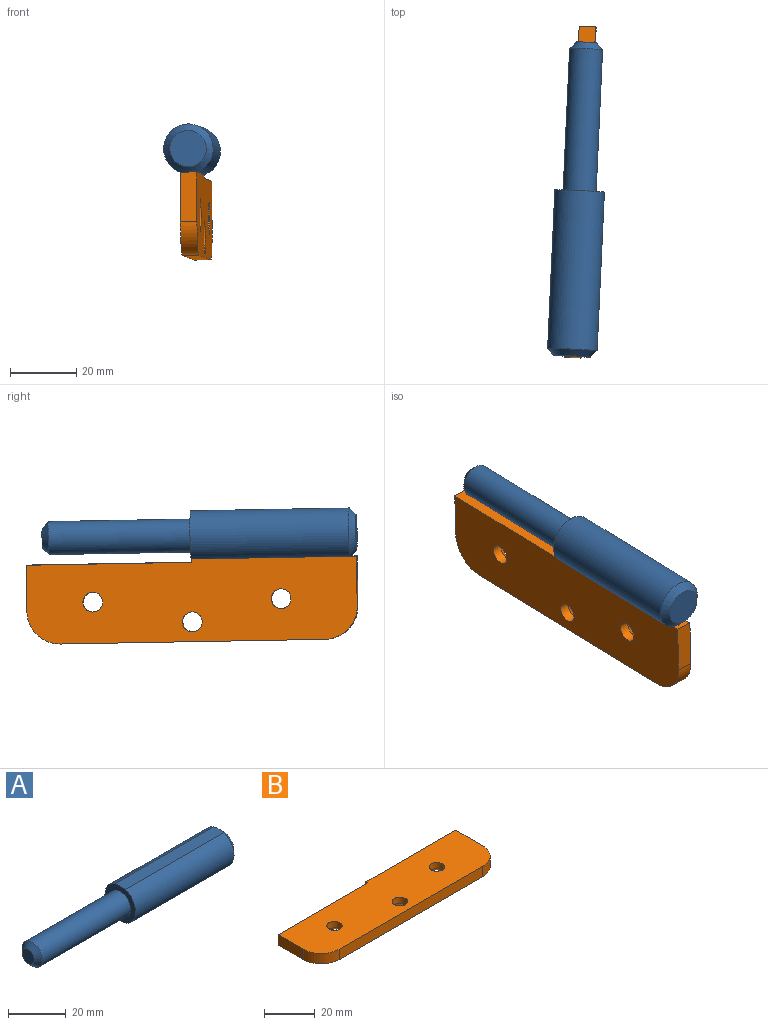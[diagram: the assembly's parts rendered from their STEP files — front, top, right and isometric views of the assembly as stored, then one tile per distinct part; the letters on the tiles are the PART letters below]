
ASSEMBLY  parts=2 mates=1
PART A: 8 faces, bbox 95x15x15 mm
  f0: cylinder r=7.5mm len=48mm, axis (-1,0,0), area 2017.3mm2, adj f2,f6,f7
  f1: plane 11x11mm, normal (1,0,0), area 95mm2, adj f7
  f2: plane 15x14.57mm, normal (-1,0,0), area 96.7mm2, adj f0,f3,f6
  f3: cylinder r=5mm len=43mm, axis (1,0,0), area 1350.9mm2, adj f2,f5
  f4: plane 6x6mm, normal (-1,0,0), area 28.3mm2, adj f5
  f5: cone r=3mm half-angle=45deg, axis (1,0,0), area 71.1mm2, adj f3,f4
  f6: plane 48.43x5.01mm, normal (0,0,1), area 241.4mm2, adj f0,f2,f7
  f7: cone r=5.5mm half-angle=45deg, axis (-1,0,0), area 113.5mm2, adj f0,f1,f6
PART B: 16 faces, bbox 100x25x5 mm
  f0: plane 80x5mm, normal (0,-1,0), area 400mm2, adj f1,f7,f8,f9
  f1: cylinder r=10mm len=10mm, axis (0,0,1), area 78.5mm2, adj f0,f2,f8,f9
  f2: plane 15x5mm, normal (1,0,0), area 75mm2, adj f1,f3,f8,f9
  f3: plane 50x5mm, normal (0,1,0), area 250mm2, adj f2,f4,f8,f9
  f4: plane 5x1mm, normal (-1,0,0), area 5mm2, adj f3,f5,f8,f9
  f5: plane 50x5mm, normal (0,1,0), area 250mm2, adj f4,f6,f8,f9
  f6: plane 14x5mm, normal (-1,0,0), area 70mm2, adj f5,f7,f8,f9
  f7: cylinder r=10mm len=10mm, axis (0,0,1), area 78.5mm2, adj f0,f6,f8,f9
  f8: plane 100x25mm, normal (0,0,-1), area 2171.5mm2, adj f0,f1,f2,f3,f4,f5,f6,f7
  f9: plane 100x25mm, normal (0,0,1), area 2322.3mm2, adj f0,f1,f2,f3,f4,f5,f6,f7
  f10: cylinder r=3mm len=6mm, axis (0,0,1), area 56.5mm2, adj f9,f15
  f11: cylinder r=3mm len=6mm, axis (0,0,1), area 56.5mm2, adj f9,f13
  f12: cylinder r=3mm len=6mm, axis (0,0,1), area 56.5mm2, adj f9,f14
  f13: cone r=5mm half-angle=45deg, axis (0,0,-1), area 71.1mm2, adj f8,f11
  f14: cone r=5mm half-angle=45deg, axis (0,0,-1), area 71.1mm2, adj f8,f12
  f15: cone r=5mm half-angle=45deg, axis (0,0,-1), area 71.1mm2, adj f8,f10
PLACE A rot(axis=(0.69,-0.72,0.01),179.6deg) t=(-69.78,49.32,-13.69)mm
PLACE B rot(axis=(0.56,-0.59,-0.58),121.2deg) t=(-72.11,49.08,-33.28)mm
MATE fastened A.f6 <-> B.f3  axis (0.01,-0.02,-1) through (-69.72,49.2,-20.76)mm
